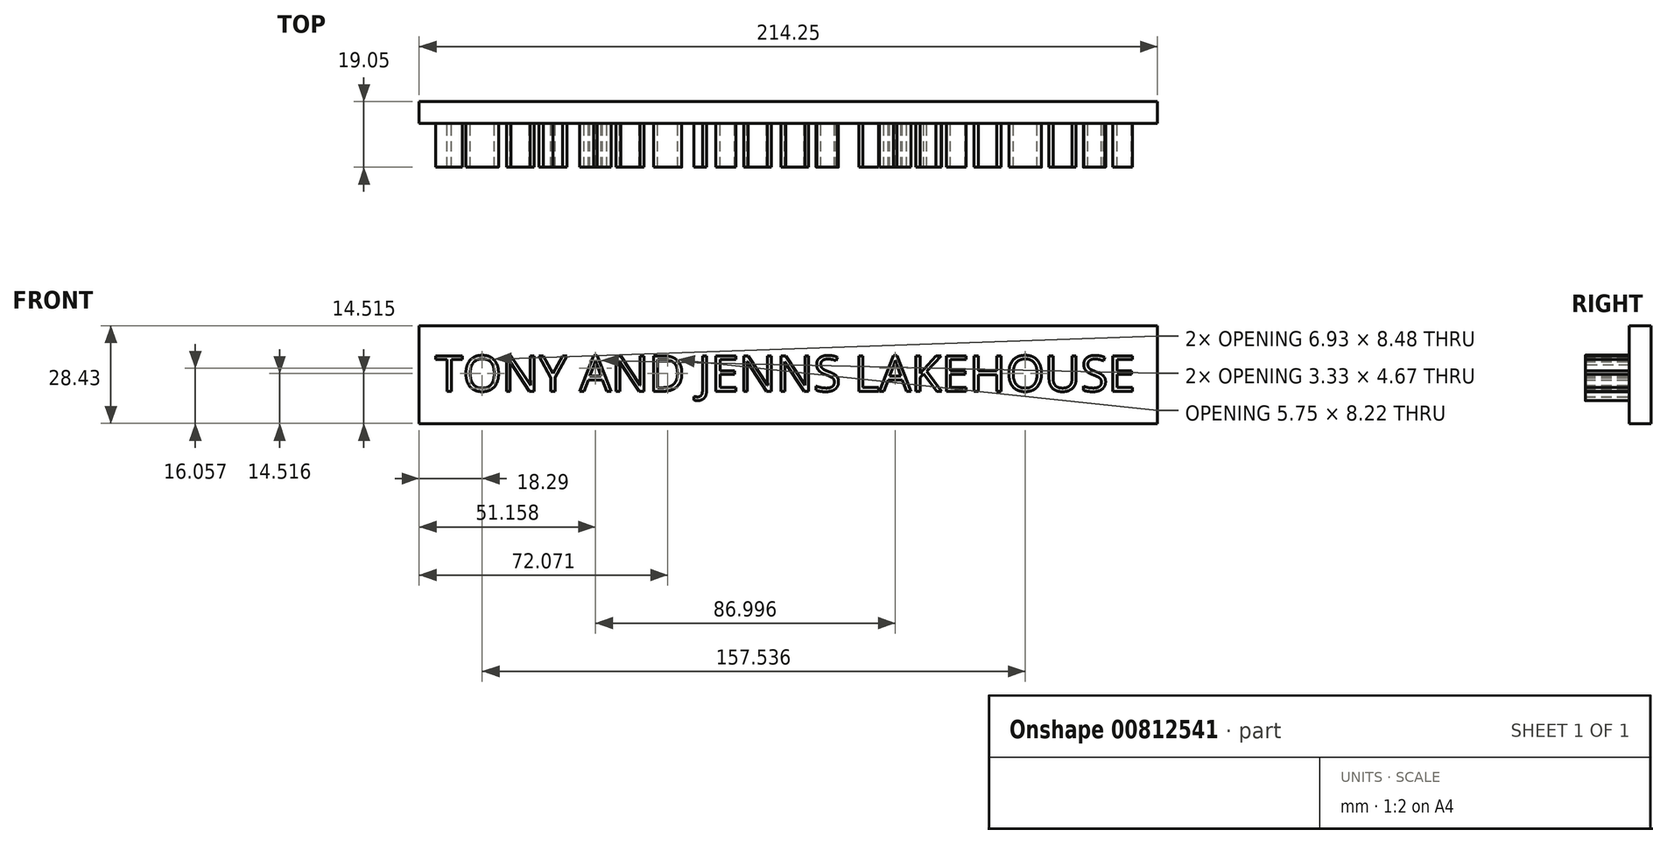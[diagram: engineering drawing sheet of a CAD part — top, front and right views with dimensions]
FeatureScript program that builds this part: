
annotation { "Feature Type Name" : "Feature", "Feature Type Description" : "" }
export const myFeature = defineFeature(function(context is Context, id is Id, definition is map)
    precondition{}
    {
        {
            var Q0;
            Q0=qCreatedBy(makeId("Front.planeOp"),FACE);
            var sketch = newSketch(context, id + "F0", { "sketchPlane" : qUnion([Q0])});
            skText(sketch, "E0", { "text": "TONY AND JENNS LAKEHOUSE\n", "fontName": "OpenSans-Regular.ttf"});
            const initialGuessF0  = {"E0": [-0.10321, -0.00494, 1, 0, 0.01038]};
            skSetInitialGuess(sketch, initialGuessF0);
            skSolve(sketch);
        }
        {
            var Q0;
            Q0 = qSketchRegion(id + "F0", true);
            extrude(context, id + "F1", {"entities" : qUnion([Q0]), "depth" : 12.7 * mm, "offsetDistance" : 25.4 * mm});
        }
        {
            var Q0;
            Q0=qCreatedBy(makeId("Front.planeOp"),FACE);
            var sketch = newSketch(context, id + "F2", { "sketchPlane" : qUnion([Q0])});
            skLineSegment(sketch, "E1.bottom", {"start": v(-107.9, 14.12) * mm, "end": v(106.34, 14.12) * mm});
            skLineSegment(sketch, "E1.top", {"start": v(-107.9, -14.31) * mm, "end": v(106.34, -14.31) * mm});
            skLineSegment(sketch, "E1.left", {"start": v(-107.9, 14.12) * mm, "end": v(-107.9, -14.31) * mm});
            skLineSegment(sketch, "E1.right", {"start": v(106.34, 14.12) * mm, "end": v(106.34, -14.31) * mm});
            skSolve(sketch);
        }
        {
            var Q0;
            Q0=makeQuery(id+"F2.imprint","IMPRINT",FACE,{"disambiguationData":[TD([[makeQuery(id+"F2.imprint","IMPRINT",EDGE,{"derivedFrom":sQuery(id+"F2.wireOp",EDGE,"E1.bottom")}),-1.0]])]});
            extrude(context, id + "F3", {"entities" : qUnion([Q0]), "depth" : -6.35 * mm, "offsetDistance" : 25.4 * mm});
        }
    });
